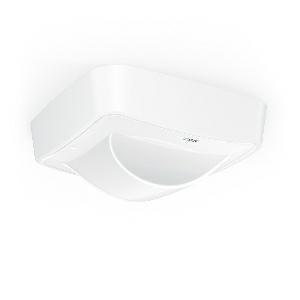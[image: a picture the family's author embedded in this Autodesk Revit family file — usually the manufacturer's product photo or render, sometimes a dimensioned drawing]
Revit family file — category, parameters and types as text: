
# Revit family: hallway_057992
name_source: partatom
category: Elektroinstallationen
revit_build: Autodesk Revit 2016 (Build: 20190508_0715(x64)
units: mm (PartAtom-declared; Revit-internal decimal feet)

## family parameters
Basisbauteil = Fläche
Beim Laden mit Abzugskörper schneiden = Nein
Bemaßung runder Anschluss = Durchmesser verwenden
Beschriftungsausrichtung beibehalten = Nein
Gemeinsam genutzt = Nein
Raumberechnungspunkt = Nein
Teiletyp = Normal

## types (1)
- Hallway
    Apparent Load = 0 VA
    Beschreibung = Type: Presence detector; Dimensions (L x W x H): 62 x 123 x 123 mm; Mains power supply: 220 – 240 V / 50 – 60 Hz; Power consumption: 0,7 W; Sensor Technology: High frequency; Application, place: Indoors; Application, room: Indoors, corridor / aisle; Installation site: ceiling; Installation: Surface wiring; HF-system: 5,8 GHz; Electronic scalability: Yes; Mechanical scalability: No; Mounting height: 2 – 4 m; Optimum mounting height: 2,8 m; Detection: also through glass, wood and stud walls; Detection angle: 360 °; Angle of aperture: 140 °; Sneak-by guard: Yes; Capability of masking out individual segments: No; Reach, radial: 25 x 3 m (75 m²); Reach, tangential: 25 x 3 m (75 m²); Twilight setting TEACH: Yes; Twilight setting: 2 – 1000 lx; Time setting: 30 sec – 30 min; Switching output 1, resistive: 2000 W; Switching output 1, number of LEDs / fluorescent lamps: 8 pcs.; Switching output 1, floating: No; Switching output 2, resistive: 230 W; Switching output 2, floating: Yes; Constant-lighting control: No; Basic light level function: No; Functions: Group parameterisation, Semi-/fully automatic, Lighting scenario, Manual ON / ON-OFF, Neighbouring-group function, Normal / test mode; Settings via: Bluetooth; With remote control: No; Interconnection: Yes; IP-rating: IP54; Material: Plastic; Ambient temperature: -20 – 50 °C; Colour: white; Colour, RAL: 9003; Manufacturer's Warranty: 5 years; Version: COM2 - Surface wiring; PU1, EAN: 4007841057992
    Height = 123 mm
    Hersteller = Steinel
    Length = 62 mm  [stored 0.203412 ft]
    Maximum range = 10.635 m
    ModVariant = Nein
    Modell = 057992
    Mounting Place = Ceiling
    Mounting Type = Surface mounted
    Number of Poles = 1
    OnlyDefault = Ja
    Power Factor = 1
    Product Name = Hallway
    Product group = Sensor-switched outdoor light
    ProductGroupID = 3
    Protection Class = Protection class
    Protection Degree = IP 54
    RlxData = <blob elided: 193585 chars, md5=dcc251d0>
    Sensor characteristics = Stretched
    Sensor type = HF
    SensorDataFile = <blob elided: 184606 chars, md5=d44d1097>
    Type of entry = Motion
    Typenbild = produkt1_057992.jpg
    Typenkommentare = Product without accessories
    URL = http://relux.com
    VarID = ---
    Voltage = 0 V
    Vorgabe-Ansicht = 1800 mm
    Weight = 0.00 kg
    Width = 123 mm

note: [stored X ft] marks values corroborated as IEEE doubles in the binary element streams (Revit-internal decimal feet)

## geometry (parser evidence)
native form markers: Sweep x13
no freeform markers — native parametric forms only
